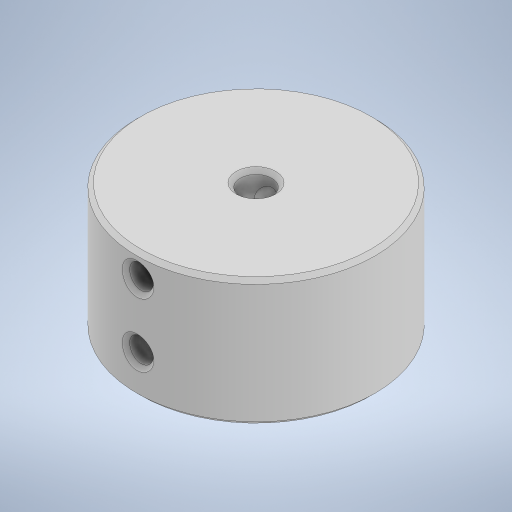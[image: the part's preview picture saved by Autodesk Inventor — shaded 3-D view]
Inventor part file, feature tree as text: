
AUTODESK INVENTOR PART (.ipt)
format: ipt  version: 2023 (Build 270158000, 158)  size: 289,792 bytes
history: native  units: mm
features: extrude x3, sketch x3, other x1, chamfer x1
ambient origin geometry x8: Origin, YZ Plane, XZ Plane, XY Plane, X Axis, Y Axis, Z Axis, Center Point
bodies: Body1 (feature_tree)
feature tree (8):
  other  "Твердое тело1"
  extrude  "Выдавливание1"  Depth=25.0mm
  extrude  "Выдавливание2"  Depth=30.0mm
  extrude  "Выдавливание3"  Depth=10.0mm TaperAngle=0.0deg
  chamfer  "Фаска1"  Distance=4.0mm
  sketch  "Эскиз1"
  sketch  "Эскиз2"
  sketch  "Эскиз3"
